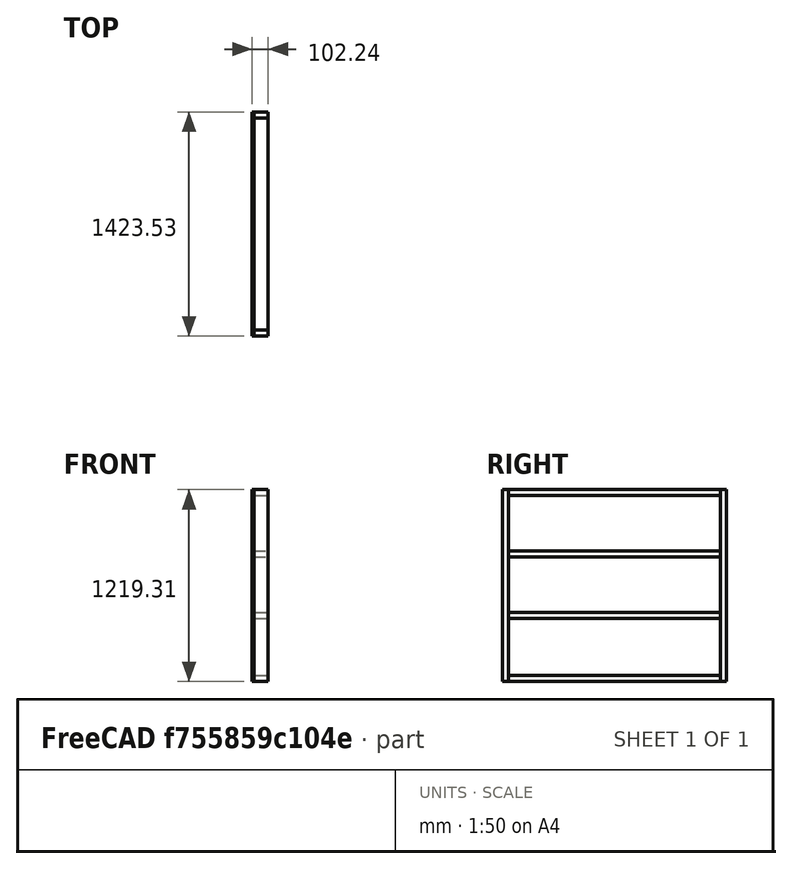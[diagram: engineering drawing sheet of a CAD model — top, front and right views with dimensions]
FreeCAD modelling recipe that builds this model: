
FCSTD DOCUMENT  (FreeCAD 0.16R6712 (Git))
Label: 4x56panel2x4
License: All rights reserved
LicenseURL: http://en.wikipedia.org/wiki/All_rights_reserved
objects: Part::FeaturePython×5, Part::Box×3, Part::Compound×1
note: 9 computed .brp shape members not serialized (recipe doc carries the construction recipe); baked Part::Feature solids carry a one-line shape summary decoded from their .brp

FEATURE [Part::Box] Box  label="Cube"
  Height = 1422.4
  Length = 12.7
  Placement = pos=(0,-441.956,-716.368) rot=(1,0,0;1.5708rad)
  Width = 1219.2
FEATURE [Part::Box] Box001  label="Cube001"
  Height = 38.1
  Length = 88.9
  Placement = pos=(12.2326,-1825.56,464.739) rot=(0,0,1;0rad)
  Width = 1346.2
FEATURE [Part::FeaturePython] Clone  label="Cube002"  # Draft clone (typed FeaturePython)
  AttacherType = Attacher::AttachEngine3D
  Fuse = false
  MapMode = -1
  Objects = -> [Box001]
  Placement = pos=(12.7605,-1825.56,-715.956) rot=(0,0,1;0rad)
  Scale = (1,1,1)
FEATURE [Part::FeaturePython] Clone002  label="Cube004"  # Draft clone (typed FeaturePython)
  AttacherType = Attacher::AttachEngine3D
  Fuse = false
  MapMode = -1
  Objects = -> [Clone]
  Placement = pos=(13.3426,-1825.56,-314.867) rot=(0,0,1;0rad)
  Scale = (1,1,1)
FEATURE [Part::FeaturePython] Clone003  label="Cube005"  # Draft clone (typed FeaturePython)
  AttacherType = Attacher::AttachEngine3D
  Fuse = false
  MapMode = -1
  Objects = -> [Clone002]
  Placement = pos=(9.2831,-1825.56,75.4186) rot=(0,0,1;0rad)
  Scale = (1,1,1)
FEATURE [Part::Box] Box002  label="Cube006"
  Height = 1219.2
  Length = 38.1
  Placement = pos=(101.576,-478.924,-716.263) rot=(0,0,1;1.5708rad)
  Width = 88.9
FEATURE [Part::FeaturePython] Clone004  label="Cube007"  # Draft clone (typed FeaturePython)
  AttacherType = Attacher::AttachEngine3D
  Fuse = false
  MapMode = -1
  Objects = -> [Box002]
  Placement = pos=(101.458,-1863.48,-716.263) rot=(0,0,1;1.5708rad)
  Scale = (1,1,1)
FEATURE [Part::Compound] Compound
  Links = -> [Box,Clone003,Box002,Clone002,Clone,Clone004,Box001]
FEATURE [Part::FeaturePython] Clone005  label="Clone of Compound"  # Draft clone (typed FeaturePython)
  Objects = -> [Compound]
  Placement = pos=(402.91,-65.8749,293.181) rot=(0,0,1;0rad)
  Scale = (1,1,1)
